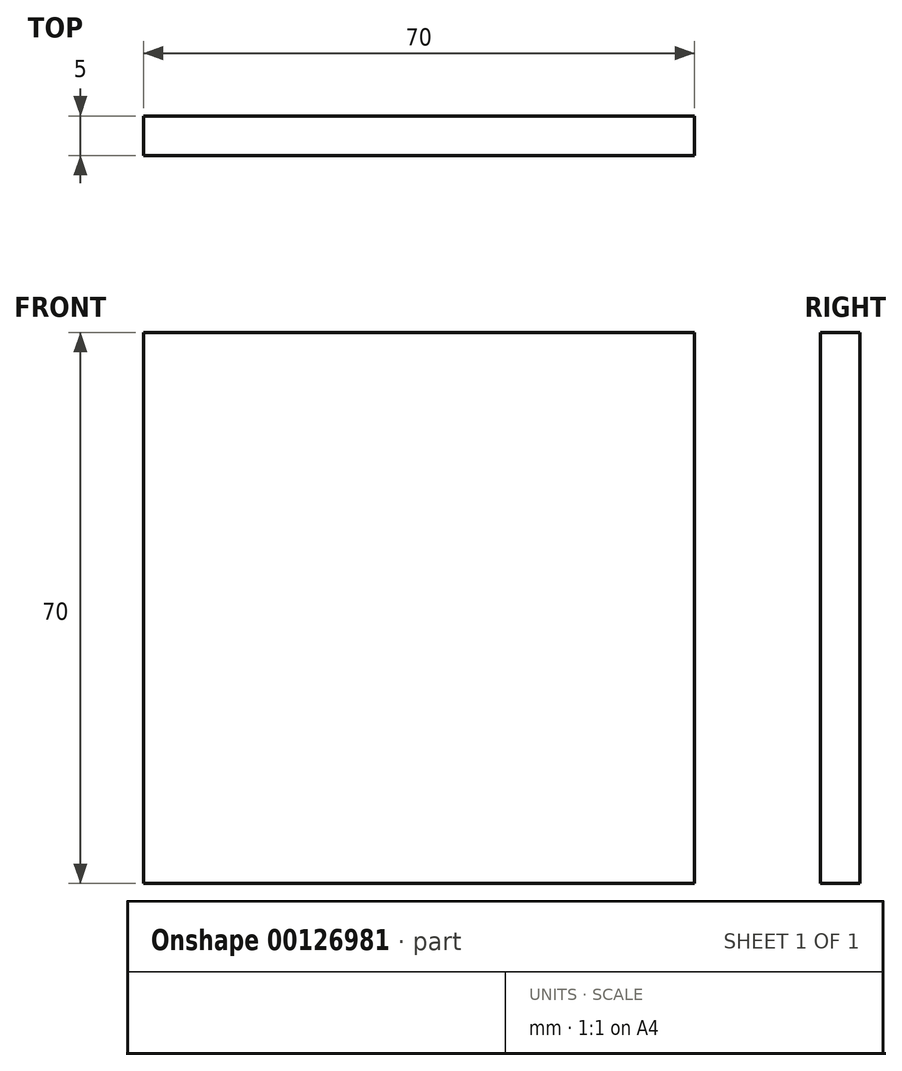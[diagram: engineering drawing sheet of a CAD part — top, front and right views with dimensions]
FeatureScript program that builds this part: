
annotation { "Feature Type Name" : "Feature", "Feature Type Description" : "" }
export const myFeature = defineFeature(function(context is Context, id is Id, definition is map)
    precondition{}
    {
        {
            var Q0;
            Q0=qCreatedBy(makeId("Front.planeOp"),FACE);
            var sketch = newSketch(context, id + "F0", { "sketchPlane" : qUnion([Q0])});
            skLineSegment(sketch, "E0.bottom", {"start": v(0, 0) * mm, "end": v(-70, 0) * mm});
            skLineSegment(sketch, "E0.top", {"start": v(0, -70) * mm, "end": v(-70, -70) * mm});
            skLineSegment(sketch, "E0.left", {"start": v(0, 0) * mm, "end": v(0, -70) * mm});
            skLineSegment(sketch, "E0.right", {"start": v(-70, 0) * mm, "end": v(-70, -70) * mm});
            skSolve(sketch);
        }
        {
            var Q0;
            Q0 = qSketchRegion(id + "F0", true);
            extrude(context, id + "F1", {"entities" : qUnion([Q0]), "depth" : 5 * mm});
        }
    });
